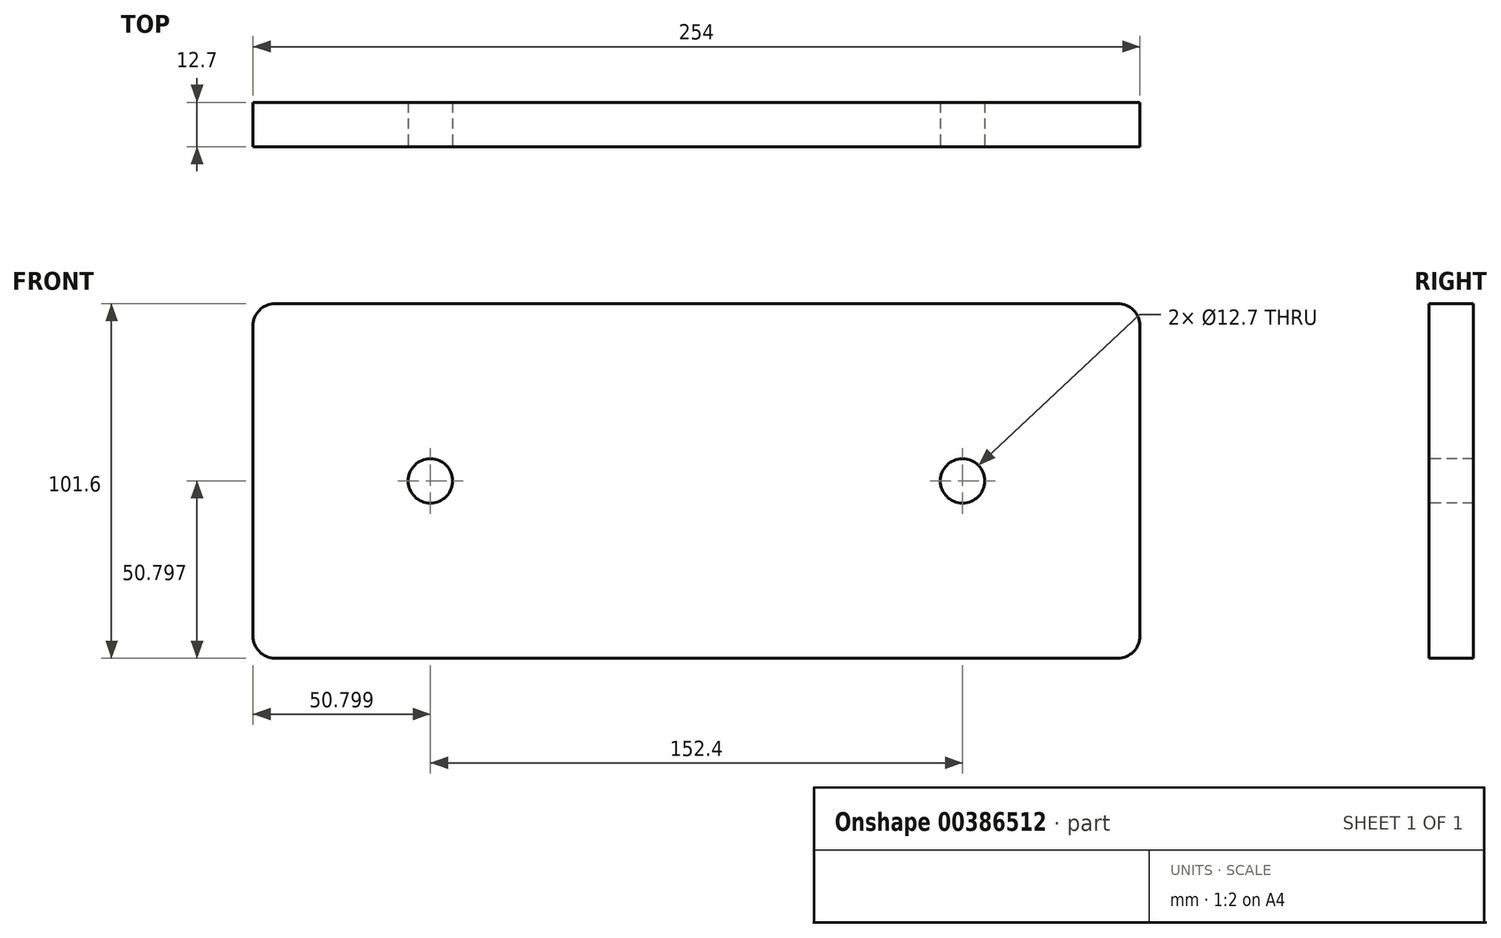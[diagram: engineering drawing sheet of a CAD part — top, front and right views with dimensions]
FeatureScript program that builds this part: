
annotation { "Feature Type Name" : "Feature", "Feature Type Description" : "" }
export const myFeature = defineFeature(function(context is Context, id is Id, definition is map)
    precondition{}
    {
        {
            var Q0;
            Q0=qCreatedBy(makeId("Front.planeOp"),FACE);
            var sketch = newSketch(context, id + "F0", { "sketchPlane" : qUnion([Q0])});
            skLineSegment(sketch, "E0.bottom", {"start": v(-92.55, -27.28) * mm, "end": v(161.45, -27.28) * mm});
            skLineSegment(sketch, "E0.top", {"start": v(-92.55, 74.32) * mm, "end": v(161.45, 74.32) * mm});
            skLineSegment(sketch, "E0.left", {"start": v(-92.55, -27.28) * mm, "end": v(-92.55, 74.32) * mm});
            skLineSegment(sketch, "E0.right", {"start": v(161.45, -27.28) * mm, "end": v(161.45, 74.32) * mm});
            skSolve(sketch);
        }
        {
            var Q0;
            Q0=makeQuery(id+"F0.imprint","IMPRINT",FACE,{"disambiguationData":[TD([[makeQuery(id+"F0.imprint","IMPRINT",EDGE,{"derivedFrom":sQuery(id+"F0.wireOp",EDGE,"E0.bottom")}),1.0]])]});
            extrude(context, id + "F1", {"entities" : qUnion([Q0]), "depth" : 12.7 * mm});
        }
        {
            var Q0;
            Q0=makeQuery(id+"F1.opExtrude","CAP_FACE",FACE,{"disambiguationData":[OSD([sQuery(id+"F0.wireOp",EDGE,"E0.bottom"),sQuery(id+"F0.wireOp",EDGE,"E0.top"),sQuery(id+"F0.wireOp",EDGE,"E0.left"),sQuery(id+"F0.wireOp",EDGE,"E0.right")])],"isStart":false});
            var sketch = newSketch(context, id + "F2", { "sketchPlane" : qUnion([Q0])});
            skPoint(sketch, "E1", {"position": v(-41.75, 23.52) * mm});
            skPoint(sketch, "E2", {"position": v(110.65, 23.52) * mm});
            skSolve(sketch);
        }
        {
            var Q0;
            Q0=sQuery(id+"F2.wireOp",VERTEX,"E1");
            var Q1;
            Q1=sQuery(id+"F2.wireOp",VERTEX,"E2");
            var Q2;
            Q2=makeQuery(id+"F1.opExtrude","SWEPT_BODY",BODY,{"disambiguationData":[OSD([sQuery(id+"F0.wireOp",EDGE,"E0.bottom"),sQuery(id+"F0.wireOp",EDGE,"E0.top"),sQuery(id+"F0.wireOp",EDGE,"E0.left"),sQuery(id+"F0.wireOp",EDGE,"E0.right")])]});
            hole(context, id + "F3", {"style" : HoleStyle.SIMPLE, "endStyle" : HoleEndStyle.THROUGH, "holeDiameter" : 12.7 * mm, "isTappedThrough" : true, "tappedDepth" : 12.7 * mm, "tapClearance" : 3, "locations" : qUnion([Q0, Q1]), "scope" : qUnion([Q2])});
        }
        {
            var Q0;
            Q0=makeQuery(id+"F1.opExtrude","SWEPT_EDGE",EDGE,{"disambiguationData":[OSD([sQuery(id+"F0.wireOp",EDGE,"E0.top"),sQuery(id+"F0.wireOp",EDGE,"E0.left")])]});
            var Q1;
            Q1=makeQuery(id+"F1.opExtrude","SWEPT_EDGE",EDGE,{"disambiguationData":[OSD([sQuery(id+"F0.wireOp",EDGE,"E0.bottom"),sQuery(id+"F0.wireOp",EDGE,"E0.left")])]});
            var Q2;
            Q2=makeQuery(id+"F1.opExtrude","SWEPT_EDGE",EDGE,{"disambiguationData":[OSD([sQuery(id+"F0.wireOp",EDGE,"E0.top"),sQuery(id+"F0.wireOp",EDGE,"E0.right")])]});
            var Q3;
            Q3=makeQuery(id+"F1.opExtrude","SWEPT_EDGE",EDGE,{"disambiguationData":[OSD([sQuery(id+"F0.wireOp",EDGE,"E0.bottom"),sQuery(id+"F0.wireOp",EDGE,"E0.right")])]});
            fillet(context, id + "F4", {"entities" : qUnion([Q0, Q1, Q2, Q3]), "radius" : 6.35 * mm, "tangentPropagation" : true, "allowEdgeOverflow" : false});
        }
    });
